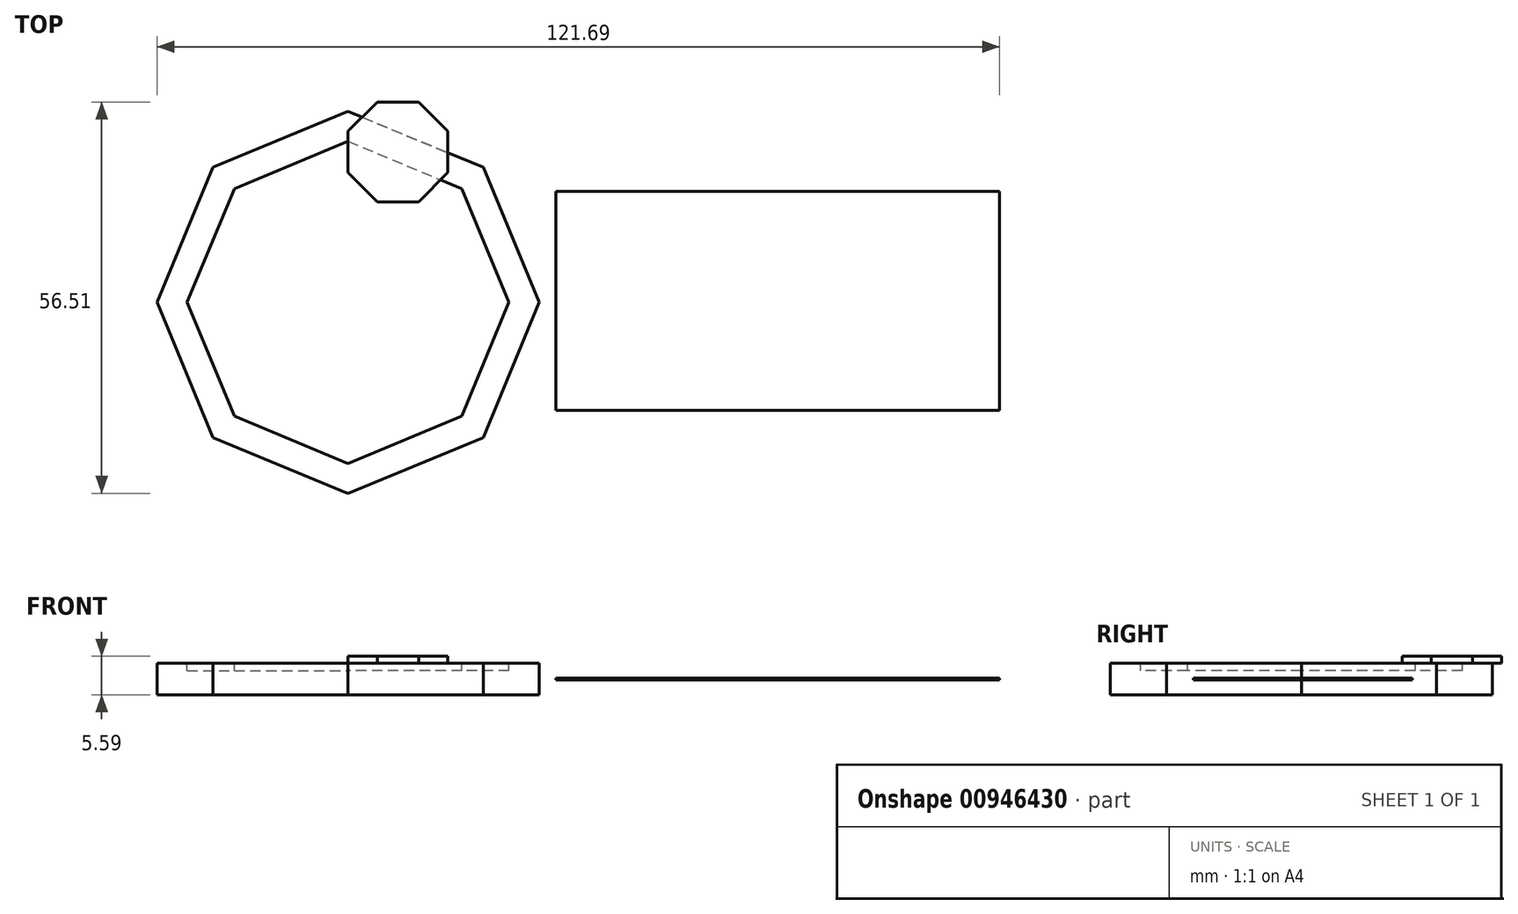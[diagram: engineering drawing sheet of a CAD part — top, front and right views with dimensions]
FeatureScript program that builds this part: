
annotation { "Feature Type Name" : "Feature", "Feature Type Description" : "" }
export const myFeature = defineFeature(function(context is Context, id is Id, definition is map)
    precondition{}
    {
        {
            var Q0;
            Q0=qCreatedBy(makeId("Top.planeOp"),FACE);
            var sketch = newSketch(context, id + "F0", { "sketchPlane" : qUnion([Q0])});
            skCircle(sketch, "E0.cCircle", {"center": v(0, 0) * mm, "radius": 25.48 * mm, "construction": true});
            skLineSegment(sketch, "E0.0", {"start": v(19.5, -19.5) * mm, "end": v(0, -27.58) * mm});
            skLineSegment(sketch, "E0.1", {"start": v(0, -27.58) * mm, "end": v(-19.5, -19.5) * mm});
            skLineSegment(sketch, "E0.2", {"start": v(-19.5, -19.5) * mm, "end": v(-27.58, 0) * mm});
            skLineSegment(sketch, "E0.3", {"start": v(-27.58, 0) * mm, "end": v(-19.5, 19.5) * mm});
            skLineSegment(sketch, "E0.4", {"start": v(-19.5, 19.5) * mm, "end": v(0, 27.58) * mm});
            skLineSegment(sketch, "E0.5", {"start": v(0, 27.58) * mm, "end": v(19.5, 19.5) * mm});
            skLineSegment(sketch, "E0.6", {"start": v(19.5, 19.5) * mm, "end": v(27.58, 0) * mm});
            skLineSegment(sketch, "E0.7", {"start": v(27.58, 0) * mm, "end": v(19.5, -19.5) * mm});
            skPoint(sketch, "E0.0.midPoint", {"position": v(9.75, -23.54) * mm});
            skSolve(sketch);
        }
        {
            var Q0;
            Q0 = qSketchRegion(id + "F0", true);
            extrude(context, id + "F1", {"entities" : qUnion([Q0]), "depth" : 4.57 * mm, "offsetDistance" : 25.4 * mm});
        }
        {
            var Q0;
            Q0=makeQuery(id+"F1.opExtrude","CAP_FACE",FACE,{"disambiguationData":[OSD([sQuery(id+"F0.wireOp",EDGE,"E0.0"),sQuery(id+"F0.wireOp",EDGE,"E0.1"),sQuery(id+"F0.wireOp",EDGE,"E0.2"),sQuery(id+"F0.wireOp",EDGE,"E0.3"),sQuery(id+"F0.wireOp",EDGE,"E0.4"),sQuery(id+"F0.wireOp",EDGE,"E0.5"),sQuery(id+"F0.wireOp",EDGE,"E0.6"),sQuery(id+"F0.wireOp",EDGE,"E0.7")])],"isStart":false});
            var sketch = newSketch(context, id + "F2", { "sketchPlane" : qUnion([Q0])});
            skCircle(sketch, "E1.cCircle", {"center": v(0, 0) * mm, "radius": 21.47 * mm, "construction": true});
            skLineSegment(sketch, "E1.0", {"start": v(16.44, -16.44) * mm, "end": v(0, -23.24) * mm});
            skLineSegment(sketch, "E1.1", {"start": v(0, -23.24) * mm, "end": v(-16.44, -16.44) * mm});
            skLineSegment(sketch, "E1.2", {"start": v(-16.44, -16.44) * mm, "end": v(-23.24, 0) * mm});
            skLineSegment(sketch, "E1.3", {"start": v(-23.24, 0) * mm, "end": v(-16.44, 16.44) * mm});
            skLineSegment(sketch, "E1.4", {"start": v(-16.44, 16.44) * mm, "end": v(0, 23.24) * mm});
            skLineSegment(sketch, "E1.5", {"start": v(0, 23.24) * mm, "end": v(16.44, 16.44) * mm});
            skLineSegment(sketch, "E1.6", {"start": v(16.44, 16.44) * mm, "end": v(23.24, 0) * mm});
            skLineSegment(sketch, "E1.7", {"start": v(23.24, 0) * mm, "end": v(16.44, -16.44) * mm});
            skPoint(sketch, "E1.0.midPoint", {"position": v(8.22, -19.84) * mm});
            skSolve(sketch);
        }
        {
            var Q0;
            Q0 = qSketchRegion(id + "F2", true);
            extrude(context, id + "F3", {"entities" : qUnion([Q0]), "operationType" : NewBodyOperationType.REMOVE, "oppositeDirection" : true, "depth" : 1.1 * mm, "offsetDistance" : 25.4 * mm});
        }
        {
            var Q0;
            Q0=qCreatedBy(makeId("Top.planeOp"),FACE);
            cPlane(context, id + "F4", {"entities" : qUnion([Q0]), "cplaneType" : CPlaneType.OFFSET, "offset" : 2.3 * mm, "width" : 152.4 * mm, "height" : 152.4 * mm});
        }
        {
            var Q0;
            Q0=qCreatedBy(id+"F4.planeOp",FACE);
            var sketch = newSketch(context, id + "F5", { "sketchPlane" : qUnion([Q0])});
            skLineSegment(sketch, "E2.bottom", {"start": v(30.02, 16.02) * mm, "end": v(94.1, 16.02) * mm});
            skLineSegment(sketch, "E2.top", {"start": v(30.02, -15.62) * mm, "end": v(94.1, -15.62) * mm});
            skLineSegment(sketch, "E2.left", {"start": v(30.02, 16.02) * mm, "end": v(30.02, -15.62) * mm});
            skLineSegment(sketch, "E2.right", {"start": v(94.1, 16.02) * mm, "end": v(94.1, -15.62) * mm});
            skSolve(sketch);
        }
        {
            var Q0;
            Q0=makeQuery(id+"F5.imprint","IMPRINT",FACE,{"disambiguationData":[TD([[makeQuery(id+"F5.imprint","IMPRINT",EDGE,{"derivedFrom":sQuery(id+"F5.wireOp",EDGE,"E2.bottom")}),-1.0]])]});
            extrude(context, id + "F6", {"entities" : qUnion([Q0]), "endBound" : BoundingType.SYMMETRIC, "depth" : 0.25 * mm, "offsetDistance" : 25.4 * mm});
        }
        {
            var Q0;
            Q0=makeQuery(id+"F1.opExtrude","CAP_FACE",FACE,{"disambiguationData":[OSD([sQuery(id+"F0.wireOp",EDGE,"E0.0"),sQuery(id+"F0.wireOp",EDGE,"E0.1"),sQuery(id+"F0.wireOp",EDGE,"E0.2"),sQuery(id+"F0.wireOp",EDGE,"E0.3"),sQuery(id+"F0.wireOp",EDGE,"E0.4"),sQuery(id+"F0.wireOp",EDGE,"E0.5"),sQuery(id+"F0.wireOp",EDGE,"E0.6"),sQuery(id+"F0.wireOp",EDGE,"E0.7")])],"isStart":false});
            var sketch = newSketch(context, id + "F7", { "sketchPlane" : qUnion([Q0])});
            skPoint(sketch, "E3.cCircle.centerSnap0", {"position": v(9.75, -23.54) * mm});
            skCircle(sketch, "E4.cCircle", {"center": v(7.2, 21.73) * mm, "radius": 7.79 * mm, "construction": true});
            skLineSegment(sketch, "E4.0", {"start": v(10.18, 14.54) * mm, "end": v(4.22, 14.54) * mm});
            skLineSegment(sketch, "E4.1", {"start": v(4.22, 14.54) * mm, "end": v(0, 18.75) * mm});
            skLineSegment(sketch, "E4.2", {"start": v(0, 18.75) * mm, "end": v(0, 24.72) * mm});
            skLineSegment(sketch, "E4.3", {"start": v(0, 24.72) * mm, "end": v(4.22, 28.93) * mm});
            skLineSegment(sketch, "E4.4", {"start": v(4.22, 28.93) * mm, "end": v(10.18, 28.93) * mm});
            skLineSegment(sketch, "E4.5", {"start": v(10.18, 28.93) * mm, "end": v(14.4, 24.72) * mm});
            skLineSegment(sketch, "E4.6", {"start": v(14.4, 24.72) * mm, "end": v(14.4, 18.75) * mm});
            skLineSegment(sketch, "E4.7", {"start": v(14.4, 18.75) * mm, "end": v(10.18, 14.54) * mm});
            skSolve(sketch);
        }
        {
            var Q0;
            {var subQ7=sQuery(id+"F7.wireOp",EDGE,"E4.3");var subQ8=sQuery(id+"F7.wireOp",EDGE,"E4.2");var subQ9=makeQuery(id+"F7.imprint","INTERSECT",VERTEX,{"derivedFrom":[subQ8,subQ7]});Q0=makeQuery(id+"F7.imprint","IMPRINT",FACE,{"disambiguationData":[TD([[makeQuery(id+"F7.imprint","IMPRINT",EDGE,{"disambiguationData":[TD([[subQ9,-1.0]])],"derivedFrom":subQ7}),-1.0]])]});}
            var Q1;
            {var subQ5=sQuery(id+"F7.wireOp",EDGE,"E4.0");Q1=makeQuery(id+"F7.imprint","IMPRINT",FACE,{"disambiguationData":[TD([[makeQuery(id+"F7.imprint","IMPRINT",EDGE,{"derivedFrom":subQ5}),-1.0]])]});}
            var Q2;
            {var subQ4=sQuery(id+"F7.wireOp",EDGE,"E4.4");Q2=makeQuery(id+"F7.imprint","IMPRINT",FACE,{"disambiguationData":[TD([[makeQuery(id+"F7.imprint","IMPRINT",EDGE,{"derivedFrom":subQ4}),-1.0]])]});}
            extrude(context, id + "F8", {"entities" : qUnion([Q0, Q1, Q2]), "operationType" : NewBodyOperationType.ADD, "depth" : 1.02 * mm, "offsetDistance" : 25.4 * mm});
        }
    });
